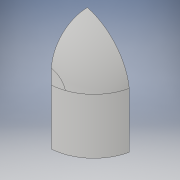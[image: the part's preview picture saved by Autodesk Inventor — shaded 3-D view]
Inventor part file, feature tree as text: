
AUTODESK INVENTOR PART (.ipt)
format: ipt  version: 2019 (Build 230136000, 136)  size: 386,048 bytes
history: native  units: mm
features: sketch x7, projected_geometry x7, extrude x4, other x1, loft x1, shell x1
ambient origin geometry x8: Origin, YZ Plane, XZ Plane, XY Plane, X Axis, Y Axis, Z Axis, Center Point
bodies: Body1 (feature_tree)
feature tree (21):
  sketch  "Эскиз3"
  sketch  "Эскиз4"
  other  "РабПлоскость1"
  loft  "Лофт1"
  extrude  "Выдавливание2"  Depth=100.0mm
  shell  "Оболочка1"  Thickness=17.0mm
  extrude  "Выдавливание3"  Depth=4.0mm
  extrude  "Выдавливание4"  Depth=35.0mm
  extrude  "Выдавливание5"  TaperAngle=0.0deg  [1 undecoded]
  sketch  "Эскиз5"
  sketch  "Эскиз6"
  projected_geometry  "Спроецированная петля1"
  sketch  "Эскиз7"
  sketch  "Эскиз8"
  sketch  "Эскиз9"
  projected_geometry  "Спроецированная петля2"
  projected_geometry  "Спроецированная петля3"
  projected_geometry  "Спроецированная петля4"
  projected_geometry  "Спроецированная петля5"
  projected_geometry  "Спроецированная петля6"
  projected_geometry  "Спроецированная петля7"
note: 1 required parameter value undecoded (feature->parameter linkage not recoverable at this tier; creation-order binding heuristic only, values carry confidence <= 0.55)
